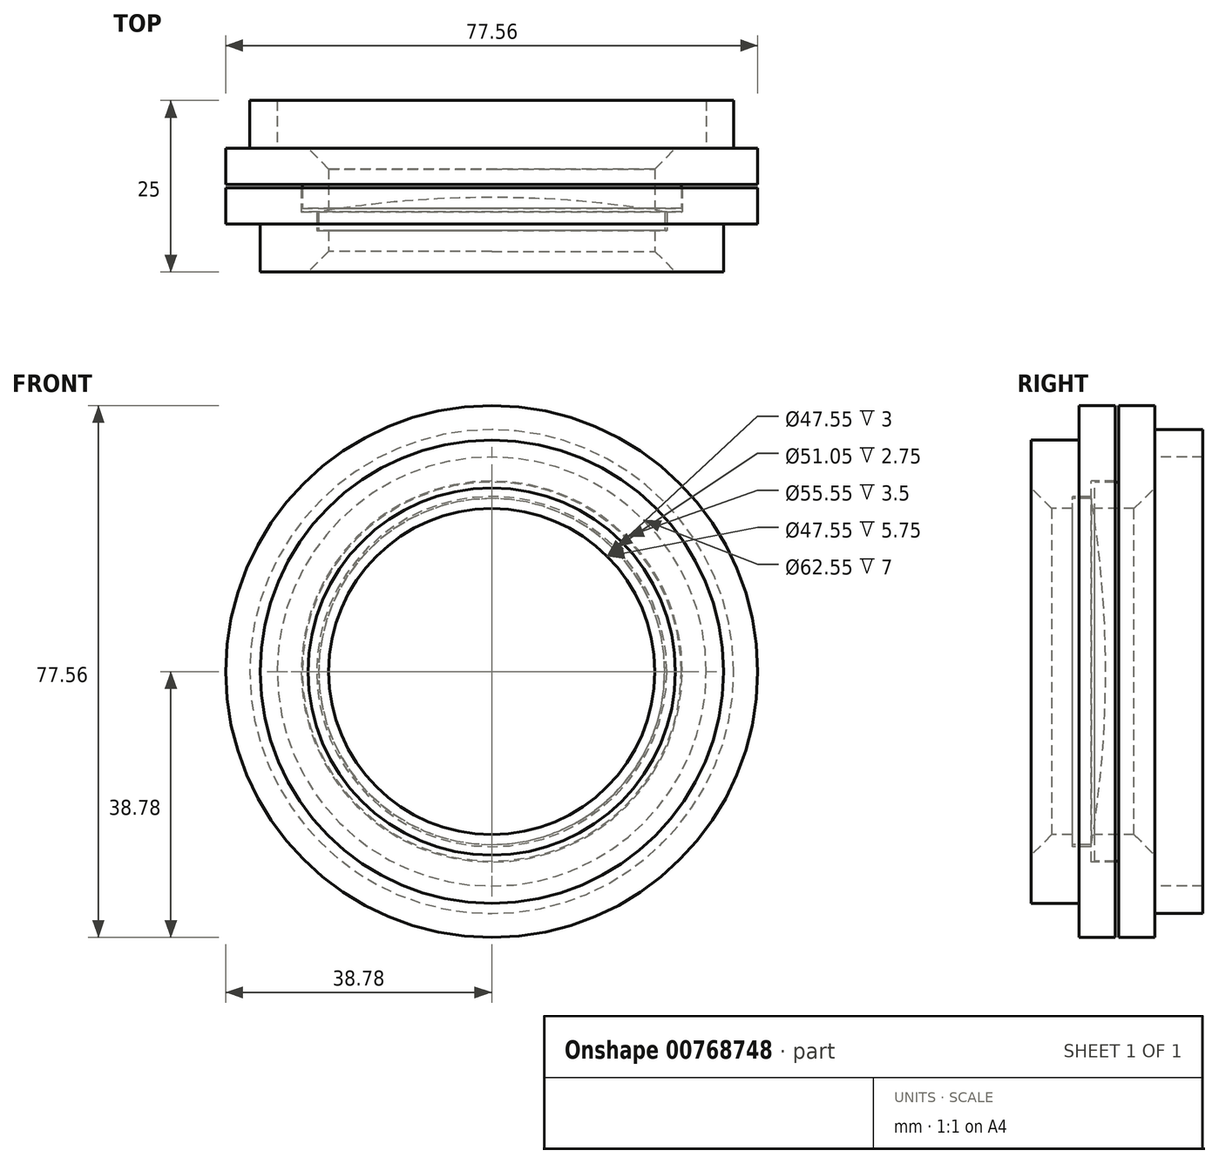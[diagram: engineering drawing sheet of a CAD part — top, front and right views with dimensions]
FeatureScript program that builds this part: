
annotation { "Feature Type Name" : "Feature", "Feature Type Description" : "" }
export const myFeature = defineFeature(function(context is Context, id is Id, definition is map)
    precondition{}
    {
        {
            var Q0;
            Q0=qCreatedBy(makeId("Right.planeOp"),FACE);
            var sketch = newSketch(context, id + "F0", { "sketchPlane" : qUnion([Q0]), "disableImprinting" : false});
            skLineSegment(sketch, "E0", {"start": v(0, 0) * mm, "end": v(0, 25.23) * mm});
            skLineSegment(sketch, "E1", {"start": v(0, 0) * mm, "end": v(4.85, 0) * mm});
            skLineSegment(sketch, "E2", {"start": v(0, 25.23) * mm, "end": v(2.75, 25.23) * mm});
            skArc(sketch, "E3", {"start": v(4.85, 0) * mm, "mid": v(4.32, 12.66) * mm, "end": v(2.75, 25.22) * mm});
            skLineSegment(sketch, "E4", {"start": v(-147.7, 0) * mm, "end": v(4.85, 0) * mm, "construction": true});
            skSolve(sketch);
        }
        {
            var Q0;
            Q0 = qSketchRegion(id + "F0", true);
            var Q1;
            Q1=sQuery(id+"F0.wireOp",EDGE,"E1");
            revolve(context, id + "F1", {"surfaceOperationType" : NewSurfaceOperationType.NEW, "entities" : qUnion([Q0]), "axis" : qUnion([Q1]), "revolveType" : RevolveType.FULL});
        }
        {
            var Q0;
            Q0=qCreatedBy(makeId("Right.planeOp"),FACE);
            var sketch = newSketch(context, id + "F2", { "sketchPlane" : qUnion([Q0]), "disableImprinting" : false});
            skLineSegment(sketch, "E5", {"start": v(-6, 33.77) * mm, "end": v(-6, 23.78) * mm});
            skLineSegment(sketch, "E6", {"start": v(-6, 23.78) * mm, "end": v(0, 23.78) * mm});
            skLineSegment(sketch, "E7", {"start": v(0, 23.78) * mm, "end": v(0, 25.53) * mm});
            skLineSegment(sketch, "E8", {"start": v(0, 25.53) * mm, "end": v(2.75, 25.53) * mm});
            skLineSegment(sketch, "E9", {"start": v(2.75, 25.53) * mm, "end": v(2.75, 27.78) * mm});
            skLineSegment(sketch, "E10", {"start": v(6.25, 38.77) * mm, "end": v(1, 38.77) * mm});
            skLineSegment(sketch, "E11", {"start": v(1, 38.77) * mm, "end": v(1, 33.77) * mm});
            skLineSegment(sketch, "E12", {"start": v(1, 33.77) * mm, "end": v(-6, 33.77) * mm});
            skLineSegment(sketch, "E13", {"start": v(2.75, 27.78) * mm, "end": v(6.25, 27.78) * mm});
            skLineSegment(sketch, "E14", {"start": v(-6, 0) * mm, "end": v(5.5, 0) * mm, "construction": true});
            skLineSegment(sketch, "E15", {"start": v(6.25, 38.77) * mm, "end": v(6.25, 27.78) * mm});
            skSolve(sketch);
        }
        {
            var Q0;
            Q0=qCreatedBy(makeId("Right.planeOp"),FACE);
            var sketch = newSketch(context, id + "F3", { "sketchPlane" : qUnion([Q0]), "disableImprinting" : false});
            skLineSegment(sketch, "E16", {"start": v(3.25, 27.63) * mm, "end": v(3.25, 23.78) * mm});
            skLineSegment(sketch, "E17", {"start": v(3.25, 23.78) * mm, "end": v(12, 23.78) * mm});
            skLineSegment(sketch, "E18", {"start": v(19, 31.27) * mm, "end": v(19, 35.27) * mm});
            skLineSegment(sketch, "E19", {"start": v(19, 35.27) * mm, "end": v(12, 35.27) * mm});
            skLineSegment(sketch, "E20", {"start": v(12, 35.27) * mm, "end": v(12, 38.78) * mm});
            skLineSegment(sketch, "E21", {"start": v(12, 38.78) * mm, "end": v(6.75, 38.78) * mm});
            skLineSegment(sketch, "E22", {"start": v(6.75, 38.78) * mm, "end": v(6.75, 27.63) * mm});
            skLineSegment(sketch, "E23", {"start": v(6.75, 27.63) * mm, "end": v(3.25, 27.63) * mm});
            skLineSegment(sketch, "E24", {"start": v(12, 23.78) * mm, "end": v(12, 31.27) * mm});
            skLineSegment(sketch, "E25", {"start": v(12, 31.27) * mm, "end": v(19, 31.27) * mm});
            skSolve(sketch);
        }
        {
            var Q0;
            Q0=makeQuery(id+"F2.imprint","IMPRINT",FACE,{"disambiguationData":[TD([[makeQuery(id+"F2.imprint","IMPRINT",EDGE,{"derivedFrom":sQuery(id+"F2.wireOp",EDGE,"E5")}),1.0]])]});
            var Q1;
            Q1=makeQuery(id+"F3.imprint","IMPRINT",FACE,{"disambiguationData":[TD([[makeQuery(id+"F3.imprint","IMPRINT",EDGE,{"derivedFrom":sQuery(id+"F3.wireOp",EDGE,"E16")}),1.0]])]});
            var Q2;
            Q2=sQuery(id+"F2.wireOp",EDGE,"E14");
            revolve(context, id + "F4", {"surfaceOperationType" : NewSurfaceOperationType.NEW, "entities" : qUnion([Q0, Q1]), "axis" : qUnion([Q2]), "revolveType" : RevolveType.FULL});
        }
        {
            var Q0;
            Q0=makeQuery(id+"F4.opRevolve","SWEPT_EDGE",EDGE,{"disambiguationData":[OSD([sQuery(id+"F2.wireOp",EDGE,"E5"),sQuery(id+"F2.wireOp",EDGE,"E6")])]});
            var Q1;
            Q1=makeQuery(id+"F4.opRevolve","SWEPT_EDGE",EDGE,{"disambiguationData":[OSD([sQuery(id+"F3.wireOp",EDGE,"E17"),sQuery(id+"F3.wireOp",EDGE,"E24")])]});
            chamfer(context, id + "F5", {"entities" : qUnion([Q0, Q1]), "width" : 3 * mm, "tangentPropagation" : true});
        }
    });
